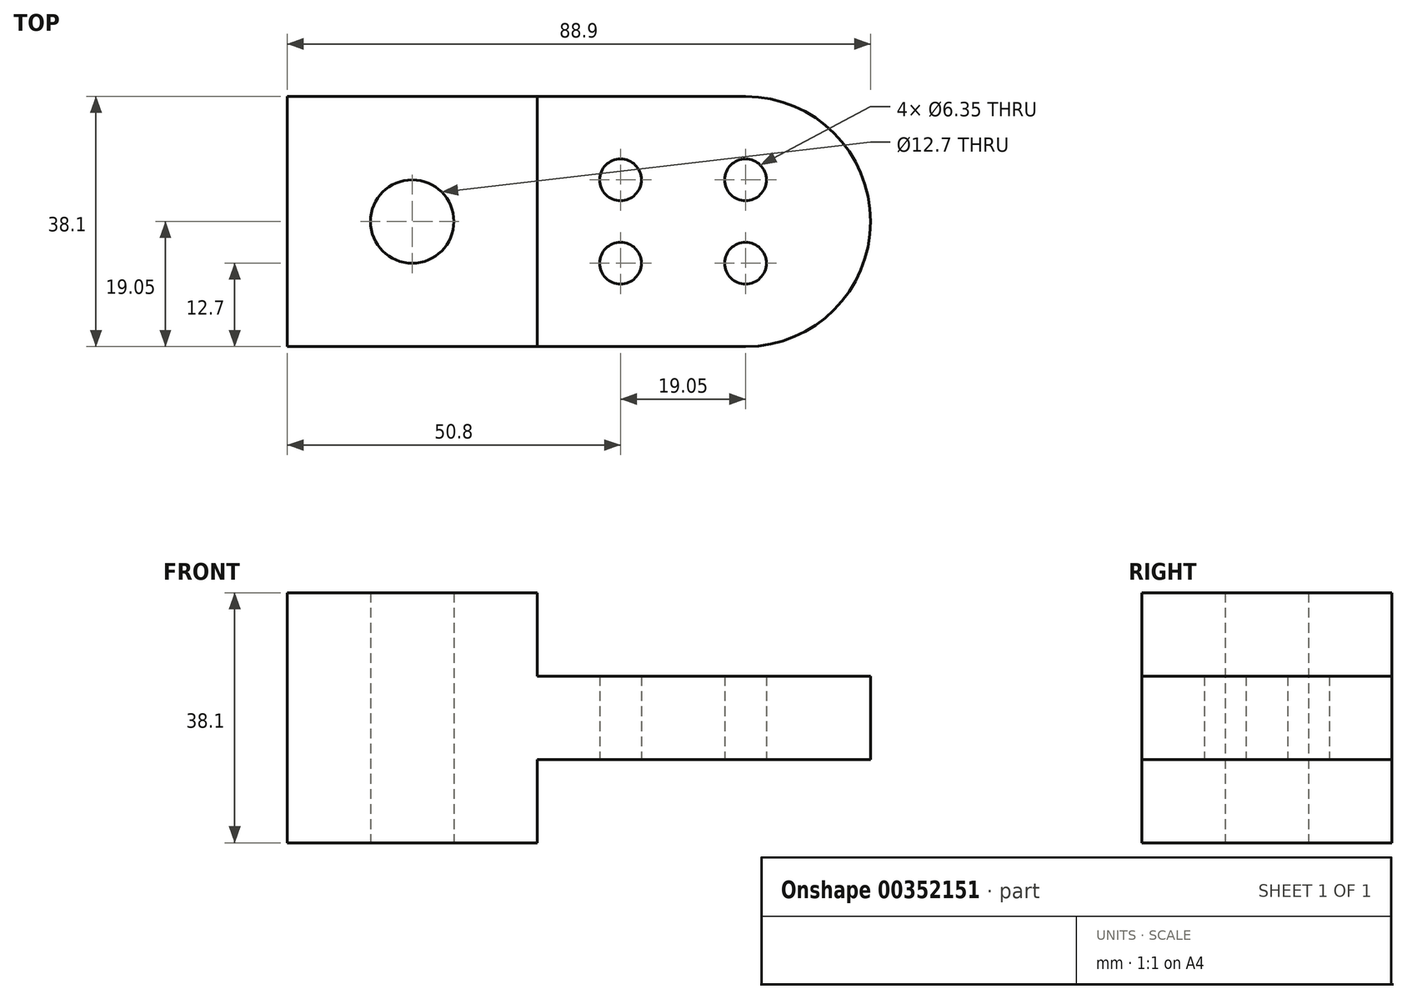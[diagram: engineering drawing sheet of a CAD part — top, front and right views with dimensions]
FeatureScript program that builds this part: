
annotation { "Feature Type Name" : "Feature", "Feature Type Description" : "" }
export const myFeature = defineFeature(function(context is Context, id is Id, definition is map)
    precondition{}
    {
        {
            var Q0;
            Q0=qCreatedBy(makeId("Top.planeOp"),FACE);
            var sketch = newSketch(context, id + "F0", { "sketchPlane" : qUnion([Q0])});
            skLineSegment(sketch, "E0.bottom", {"start": v(0, 0) * mm, "end": v(38.1, 0) * mm});
            skLineSegment(sketch, "E0.top", {"start": v(0, 38.1) * mm, "end": v(38.1, 38.1) * mm});
            skLineSegment(sketch, "E0.left", {"start": v(0, 0) * mm, "end": v(0, 38.1) * mm});
            skLineSegment(sketch, "E0.right", {"start": v(38.1, 0) * mm, "end": v(38.1, 38.1) * mm});
            skLineSegment(sketch, "E1.bottom", {"start": v(38.1, 38.1) * mm, "end": v(69.85, 38.1) * mm});
            skLineSegment(sketch, "E1.top", {"start": v(38.1, 0) * mm, "end": v(69.85, 0) * mm});
            skLineSegment(sketch, "E1.left", {"start": v(38.1, 38.1) * mm, "end": v(38.1, 0) * mm});
            skArc(sketch, "E2", {"start": v(69.85, 0) * mm, "mid": v(88.9, 19.05) * mm, "end": v(69.85, 38.1) * mm});
            skCircle(sketch, "E3", {"center": v(19.05, 19.05) * mm, "radius": 6.35 * mm});
            skPoint(sketch, "E3.centerSnap0", {"position": v(0, 19.05) * mm});
            skPoint(sketch, "E3.centerSnap1", {"position": v(19.05, 38.1) * mm});
            skCircle(sketch, "E4", {"center": v(69.85, 25.4) * mm, "radius": 3.18 * mm});
            skCircle(sketch, "E5", {"center": v(69.85, 12.7) * mm, "radius": 3.18 * mm});
            skCircle(sketch, "E6", {"center": v(50.8, 25.4) * mm, "radius": 3.18 * mm});
            skCircle(sketch, "E7", {"center": v(50.8, 12.7) * mm, "radius": 3.18 * mm});
            skSolve(sketch);
        }
        {
            var Q0;
            Q0=qSketchRegion(id+"F0",true);
            extrude(context, id + "F1", {"entities" : qUnion([Q0]), "depth" : 38.1 * mm});
        }
        {
            var Q0;
            Q0=makeQuery(id+"F0.imprint","IMPRINT",FACE,{"disambiguationData":[TD([[makeQuery(id+"F0.imprint","IMPRINT",EDGE,{"derivedFrom":sQuery(id+"F0.wireOp",EDGE,"E1.bottom")}),-1.0]])]});
            extrude(context, id + "F2", {"entities" : qUnion([Q0]), "operationType" : NewBodyOperationType.REMOVE, "depth" : 12.7 * mm});
        }
        {
            var Q0;
            Q0=makeQuery(id+"F1.opExtrude","CAP_FACE",FACE,{"disambiguationData":[OSD([sQuery(id+"F0.wireOp",EDGE,"E0.bottom"),sQuery(id+"F0.wireOp",EDGE,"E0.top"),sQuery(id+"F0.wireOp",EDGE,"E0.left"),sQuery(id+"F0.wireOp",EDGE,"E1.bottom"),sQuery(id+"F0.wireOp",EDGE,"E1.top"),sQuery(id+"F0.wireOp",EDGE,"E2"),sQuery(id+"F0.wireOp",EDGE,"E3"),sQuery(id+"F0.wireOp",EDGE,"E4"),sQuery(id+"F0.wireOp",EDGE,"E5"),sQuery(id+"F0.wireOp",EDGE,"E6"),sQuery(id+"F0.wireOp",EDGE,"E7")])],"isStart":false});
            var sketch = newSketch(context, id + "F3", { "sketchPlane" : qUnion([Q0])});
            skLineSegment(sketch, "E8", {"start": v(38.1, 38.1) * mm, "end": v(38.1, 0) * mm});
            skPoint(sketch, "E9", {"position": v(0, 38.1) * mm});
            skSolve(sketch);
        }
        {
            var Q0;
            {var subQ1=sQuery(id+"F3.wireOp",EDGE,"E8");Q0=makeQuery(id+"F3.imprint","IMPRINT",FACE,{"disambiguationData":[TD([[makeQuery(id+"F3.imprint","IMPRINT",EDGE,{"derivedFrom":subQ1}),1.0]])]});}
            extrude(context, id + "F4", {"entities" : qUnion([Q0]), "operationType" : NewBodyOperationType.REMOVE, "oppositeDirection" : true, "depth" : 12.7 * mm});
        }
    });
